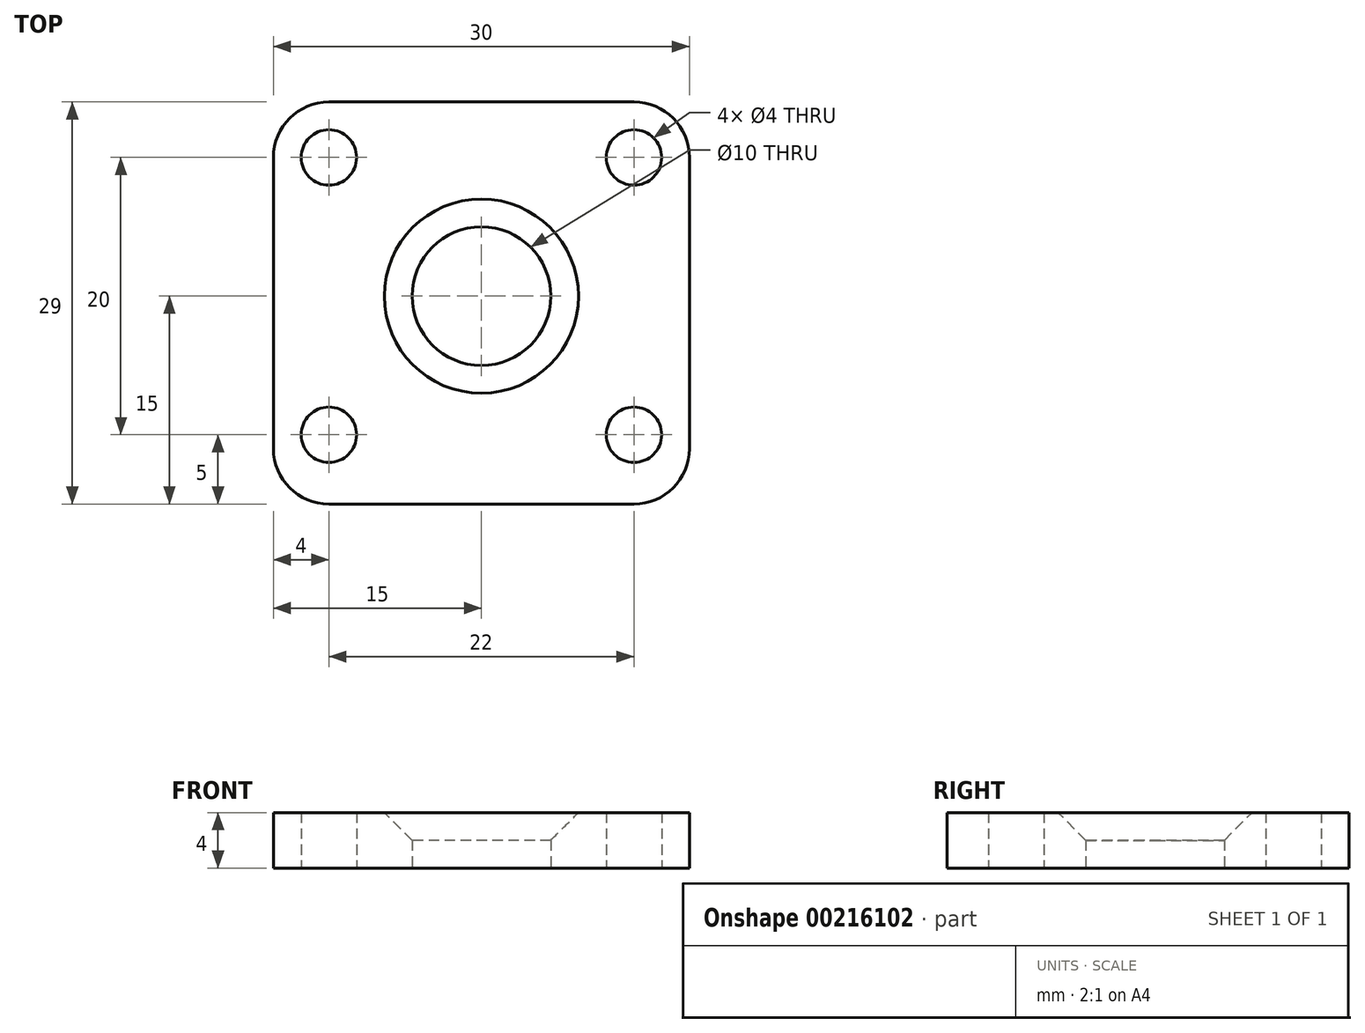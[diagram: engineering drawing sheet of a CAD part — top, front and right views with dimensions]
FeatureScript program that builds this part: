
annotation { "Feature Type Name" : "Feature", "Feature Type Description" : "" }
export const myFeature = defineFeature(function(context is Context, id is Id, definition is map)
    precondition{}
    {
        {
            var Q0;
            Q0=qCreatedBy(makeId("Top.planeOp"),FACE);
            var sketch = newSketch(context, id + "F0", { "sketchPlane" : qUnion([Q0])});
            skLineSegment(sketch, "E0.bottom", {"start": v(-15, 14) * mm, "end": v(15, 14) * mm});
            skLineSegment(sketch, "E0.top", {"start": v(-15, -15) * mm, "end": v(15, -15) * mm});
            skLineSegment(sketch, "E0.left", {"start": v(-15, 14) * mm, "end": v(-15, -15) * mm});
            skLineSegment(sketch, "E0.right", {"start": v(15, 14) * mm, "end": v(15, -15) * mm});
            skCircle(sketch, "E1", {"center": v(0, 0) * mm, "radius": 5 * mm});
            skCircle(sketch, "E2", {"center": v(-11, 10) * mm, "radius": 2 * mm});
            skCircle(sketch, "E3", {"center": v(11, 10) * mm, "radius": 2 * mm});
            skCircle(sketch, "E4", {"center": v(-11, -10) * mm, "radius": 2 * mm});
            skCircle(sketch, "E5", {"center": v(11, -10) * mm, "radius": 2 * mm});
            skSolve(sketch);
        }
        {
            var Q0;
            Q0 = qSketchRegion(id + "F0", true);
            extrude(context, id + "F1", {"entities" : qUnion([Q0]), "depth" : 4 * mm});
        }
        {
            var Q0;
            Q0=makeQuery(id+"F1.opExtrude","SWEPT_EDGE",EDGE,{"disambiguationData":[OSD([sQuery(id+"F0.wireOp",EDGE,"E0.bottom"),sQuery(id+"F0.wireOp",EDGE,"E0.left")])]});
            var Q1;
            Q1=makeQuery(id+"F1.opExtrude","SWEPT_EDGE",EDGE,{"disambiguationData":[OSD([sQuery(id+"F0.wireOp",EDGE,"E0.bottom"),sQuery(id+"F0.wireOp",EDGE,"E0.right")])]});
            var Q2;
            Q2=makeQuery(id+"F1.opExtrude","SWEPT_EDGE",EDGE,{"disambiguationData":[OSD([sQuery(id+"F0.wireOp",EDGE,"E0.top"),sQuery(id+"F0.wireOp",EDGE,"E0.left")])]});
            var Q3;
            Q3=makeQuery(id+"F1.opExtrude","SWEPT_EDGE",EDGE,{"disambiguationData":[OSD([sQuery(id+"F0.wireOp",EDGE,"E0.top"),sQuery(id+"F0.wireOp",EDGE,"E0.right")])]});
            fillet(context, id + "F2", {"entities" : qUnion([Q0, Q1, Q2, Q3]), "radius" : 4 * mm, "tangentPropagation" : true, "allowEdgeOverflow" : false});
        }
        {
            var Q0;
            Q0=makeQuery(id+"F1.opExtrude","CAP_EDGE",EDGE,{"disambiguationData":[OSD([sQuery(id+"F0.wireOp",EDGE,"E1")])],"isStart":false});
            chamfer(context, id + "F3", {"entities" : qUnion([Q0]), "width" : 2 * mm, "tangentPropagation" : true});
        }
    });
